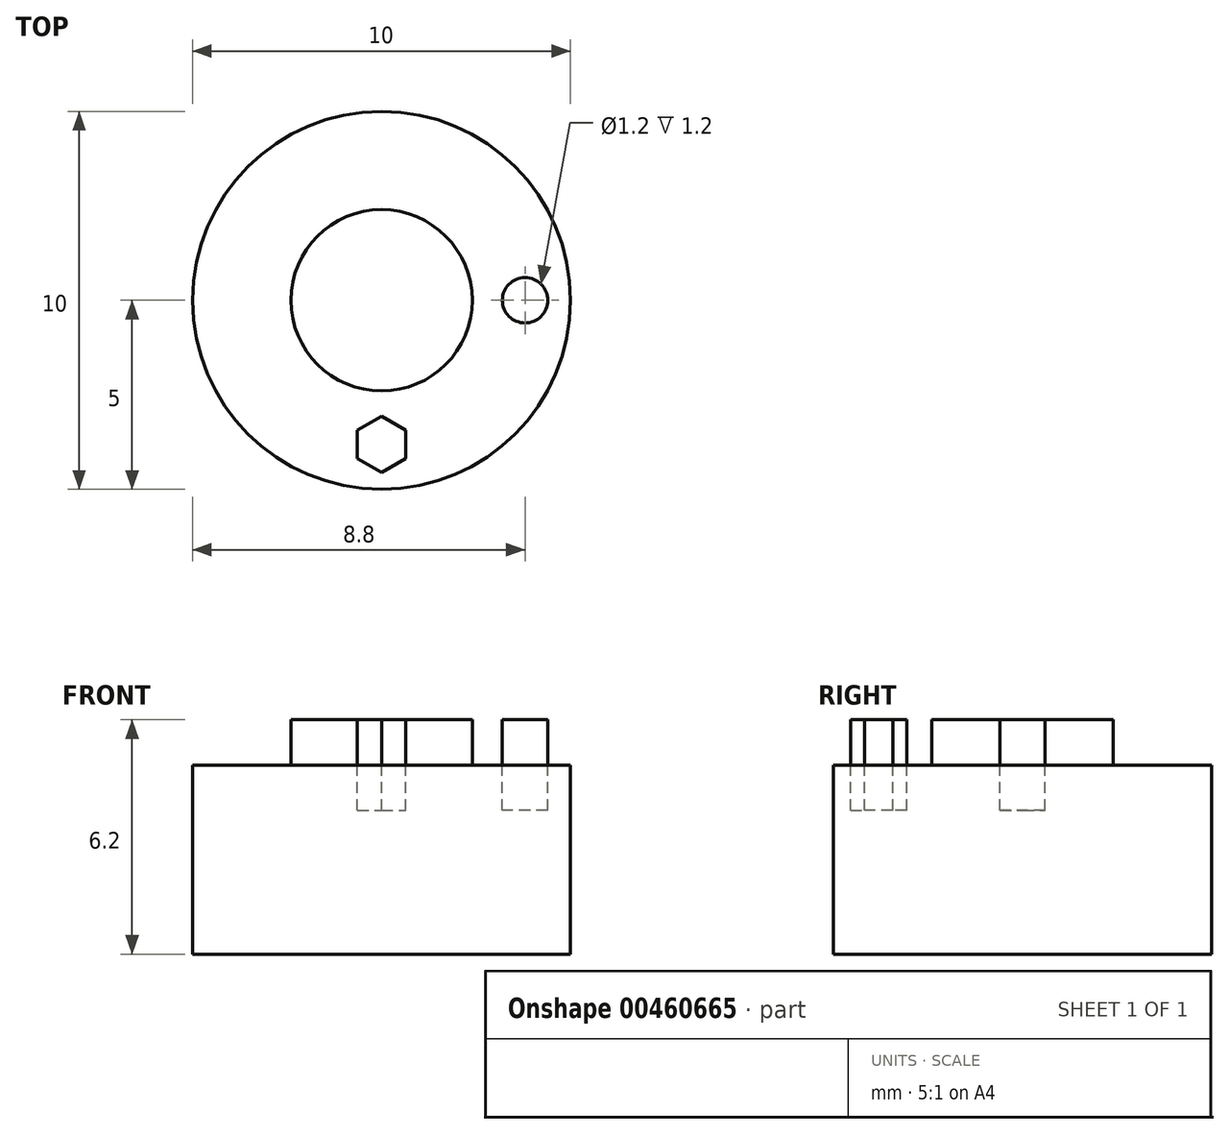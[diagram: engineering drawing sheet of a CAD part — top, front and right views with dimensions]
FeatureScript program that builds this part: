
annotation { "Feature Type Name" : "Feature", "Feature Type Description" : "" }
export const myFeature = defineFeature(function(context is Context, id is Id, definition is map)
    precondition{}
    {
        {
            var Q0;
            Q0=qCreatedBy(makeId("Top.planeOp"),FACE);
            var sketch = newSketch(context, id + "F0", { "sketchPlane" : qUnion([Q0])});
            skCircle(sketch, "E0", {"center": v(-10.54, 0) * mm, "radius": 5 * mm});
            skSolve(sketch);
        }
        {
            var Q0;
            Q0=makeQuery(id+"F0.imprint","IMPRINT",FACE,{"disambiguationData":[TD([[makeQuery(id+"F0.imprint","IMPRINT",EDGE,{"derivedFrom":sQuery(id+"F0.wireOp",EDGE,"E0")}),1.0]])]});
            extrude(context, id + "F1", {"entities" : qUnion([Q0]), "depth" : 5 * mm});
        }
        {
            var Q0;
            Q0=makeQuery(id+"F1.opExtrude","CAP_FACE",FACE,{"disambiguationData":[OSD([sQuery(id+"F0.wireOp",EDGE,"E0")])],"isStart":false});
            var sketch = newSketch(context, id + "F2", { "sketchPlane" : qUnion([Q0])});
            skCircle(sketch, "E1", {"center": v(-10.54, 0) * mm, "radius": 2.4 * mm});
            skCircle(sketch, "E2", {"center": v(-6.74, 0) * mm, "radius": 0.6 * mm});
            skCircle(sketch, "E3.cCircle", {"center": v(-10.54, -3.8) * mm, "radius": 0.65 * mm, "construction": true});
            skLineSegment(sketch, "E3.0", {"start": v(-9.9, -3.44) * mm, "end": v(-9.9, -4.18) * mm});
            skLineSegment(sketch, "E3.1", {"start": v(-9.9, -4.18) * mm, "end": v(-10.54, -4.55) * mm});
            skLineSegment(sketch, "E3.2", {"start": v(-10.54, -4.55) * mm, "end": v(-11.18, -4.18) * mm});
            skLineSegment(sketch, "E3.3", {"start": v(-11.18, -4.18) * mm, "end": v(-11.18, -3.44) * mm});
            skLineSegment(sketch, "E3.4", {"start": v(-11.18, -3.44) * mm, "end": v(-10.54, -3.06) * mm});
            skLineSegment(sketch, "E3.5", {"start": v(-10.54, -3.06) * mm, "end": v(-9.9, -3.44) * mm});
            skPoint(sketch, "E3.0.midPoint", {"position": v(-9.9, -3.8) * mm});
            skSolve(sketch);
        }
        {
            var Q0;
            Q0=makeQuery(id+"F2.imprint","IMPRINT",FACE,{"disambiguationData":[TD([[makeQuery(id+"F2.imprint","IMPRINT",EDGE,{"derivedFrom":sQuery(id+"F2.wireOp",EDGE,"E2")}),1.0]])]});
            var Q1;
            Q1=makeQuery(id+"F2.imprint","IMPRINT",FACE,{"disambiguationData":[TD([[makeQuery(id+"F2.imprint","IMPRINT",EDGE,{"derivedFrom":sQuery(id+"F2.wireOp",EDGE,"E3.0")}),-1.0]])]});
            var Q2;
            Q2=sQuery(id+"F2.wireOp",EDGE,"E1");
            extrude(context, id + "F3", {"entities" : qUnion([Q0, Q1]), "operationType" : NewBodyOperationType.REMOVE, "surfaceEntities" : qUnion([Q2]), "oppositeDirection" : true, "depth" : 1.2 * mm});
        }
        {
            var Q0;
            Q0 = qSketchRegion(id + "F2", true);
            var Q1;
            Q1=sQuery(id+"F2.wireOp",EDGE,"E2");
            extrude(context, id + "F4", {"entities" : qUnion([Q0]), "operationType" : NewBodyOperationType.ADD, "surfaceEntities" : qUnion([Q1]), "depth" : 1.2 * mm});
        }
    });
